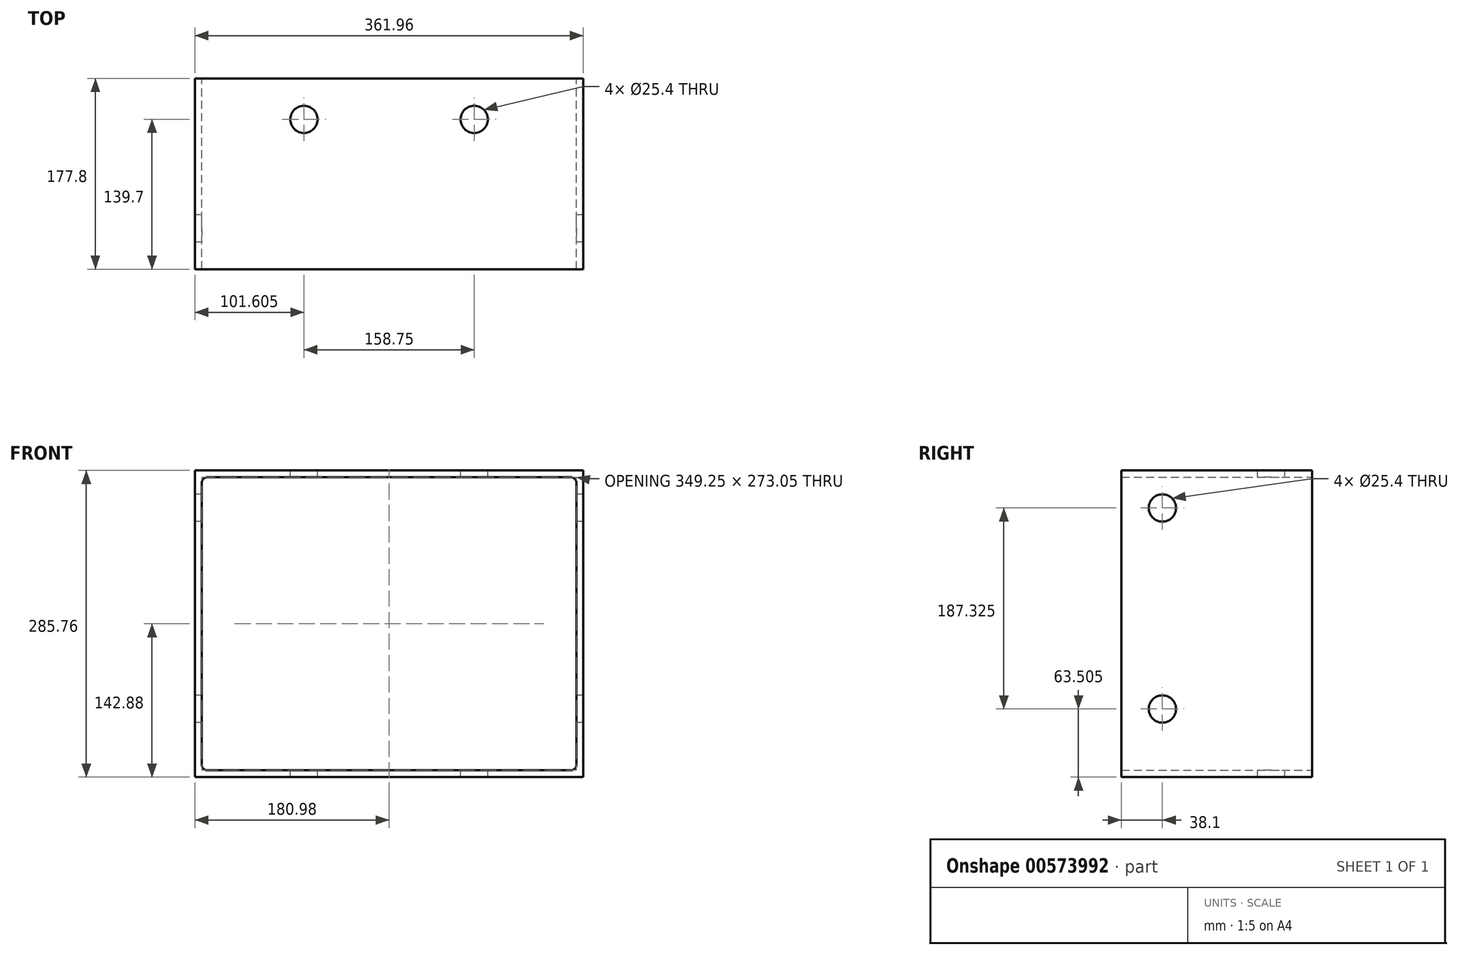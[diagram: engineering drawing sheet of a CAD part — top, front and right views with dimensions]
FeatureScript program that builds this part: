
annotation { "Feature Type Name" : "Feature", "Feature Type Description" : "" }
export const myFeature = defineFeature(function(context is Context, id is Id, definition is map)
    precondition{}
    {
        {
            var Q0;
            Q0=qCreatedBy(makeId("Front.planeOp"),FACE);
            var sketch = newSketch(context, id + "F0", { "sketchPlane" : qUnion([Q0])});
            skLineSegment(sketch, "E0.bottom", {"start": v(174.62, 136.53) * mm, "end": v(-174.63, 136.53) * mm});
            skLineSegment(sketch, "E0.top", {"start": v(174.63, -136.53) * mm, "end": v(-174.63, -136.53) * mm});
            skLineSegment(sketch, "E0.left", {"start": v(174.62, 136.53) * mm, "end": v(174.63, -136.52) * mm});
            skLineSegment(sketch, "E0.right", {"start": v(-174.63, 136.52) * mm, "end": v(-174.63, -136.53) * mm});
            skPoint(sketch, "E0.middle", {"position": v(0, 0) * mm});
            skLineSegment(sketch, "E1.bottom", {"start": v(-180.98, -142.88) * mm, "end": v(180.97, -142.88) * mm});
            skLineSegment(sketch, "E1.top", {"start": v(-180.97, 142.88) * mm, "end": v(180.98, 142.88) * mm});
            skLineSegment(sketch, "E1.left", {"start": v(-180.98, -142.88) * mm, "end": v(-180.97, 142.88) * mm});
            skLineSegment(sketch, "E1.right", {"start": v(180.98, -142.88) * mm, "end": v(180.98, 142.87) * mm});
            skSolve(sketch);
        }
        {
            var Q0;
            Q0=makeQuery(id+"F0.imprint","IMPRINT",FACE,{"disambiguationData":[TD([[makeQuery(id+"F0.imprint","IMPRINT",EDGE,{"derivedFrom":sQuery(id+"F0.wireOp",EDGE,"E0.bottom")}),-1.0]])]});
            extrude(context, id + "F1", {"entities" : qUnion([Q0]), "endBound" : BoundingType.SYMMETRIC, "depth" : 177.8 * mm, "offsetDistance" : 25.4 * mm});
        }
        {
            var Q0;
            Q0=makeQuery(id+"F1.opExtrude","SWEPT_EDGE",EDGE,{"disambiguationData":[OSD([sQuery(id+"F0.wireOp",EDGE,"E0.top"),sQuery(id+"F0.wireOp",EDGE,"E0.right")])]});
            var Q1;
            Q1=makeQuery(id+"F1.opExtrude","SWEPT_EDGE",EDGE,{"disambiguationData":[OSD([sQuery(id+"F0.wireOp",EDGE,"E0.top"),sQuery(id+"F0.wireOp",EDGE,"E0.left")])]});
            var Q2;
            Q2=makeQuery(id+"F1.opExtrude","SWEPT_EDGE",EDGE,{"disambiguationData":[OSD([sQuery(id+"F0.wireOp",EDGE,"E0.bottom"),sQuery(id+"F0.wireOp",EDGE,"E0.left")])]});
            var Q3;
            Q3=makeQuery(id+"F1.opExtrude","SWEPT_EDGE",EDGE,{"disambiguationData":[OSD([sQuery(id+"F0.wireOp",EDGE,"E0.bottom"),sQuery(id+"F0.wireOp",EDGE,"E0.right")])]});
            fillet(context, id + "F2", {"entities" : qUnion([Q0, Q1, Q2, Q3]), "radius" : 5.08 * mm, "tangentPropagation" : true, "allowEdgeOverflow" : false});
        }
        {
            var Q0;
            Q0=makeQuery(id+"F1.opExtrude","SWEPT_FACE",FACE,{"disambiguationData":[OSD([sQuery(id+"F0.wireOp",EDGE,"E1.top")])]});
            var sketch = newSketch(context, id + "F3", { "sketchPlane" : qUnion([Q0])});
            skCircle(sketch, "E2", {"center": v(-79.38, 50.8) * mm, "radius": 12.7 * mm});
            skCircle(sketch, "E3", {"center": v(79.38, 50.8) * mm, "radius": 12.7 * mm});
            skCircle(sketch, "E4", {"center": v(-79.38, 50.8) * mm, "radius": 50.8 * mm, "construction": true});
            skCircle(sketch, "E5", {"center": v(79.38, 50.8) * mm, "radius": 50.8 * mm, "construction": true});
            skSolve(sketch);
        }
        {
            var Q0;
            Q0=sQuery(id+"F3.wireOp",VERTEX,"E2.center");
            var Q1;
            Q1=sQuery(id+"F3.wireOp",VERTEX,"E3.center");
            var Q2;
            Q2=makeQuery(id+"F1.opExtrude","SWEPT_BODY",BODY,{"disambiguationData":[OSD([sQuery(id+"F0.wireOp",EDGE,"E0.bottom"),sQuery(id+"F0.wireOp",EDGE,"E0.top"),sQuery(id+"F0.wireOp",EDGE,"E0.left"),sQuery(id+"F0.wireOp",EDGE,"E0.right"),sQuery(id+"F0.wireOp",EDGE,"E1.bottom"),sQuery(id+"F0.wireOp",EDGE,"E1.top"),sQuery(id+"F0.wireOp",EDGE,"E1.left"),sQuery(id+"F0.wireOp",EDGE,"E1.right")])]});
            hole(context, id + "F4", {"style" : HoleStyle.SIMPLE, "endStyle" : HoleEndStyle.THROUGH, "holeDiameter" : 25.4 * mm, "isTappedThrough" : true, "tappedDepth" : 12.7 * mm, "tapClearance" : 3, "locations" : qUnion([Q0, Q1]), "scope" : qUnion([Q2]), "majorDiameter" : 6.35 * mm});
        }
        {
            var Q0;
            Q0=makeQuery(id+"F1.opExtrude","SWEPT_FACE",FACE,{"disambiguationData":[OSD([sQuery(id+"F0.wireOp",EDGE,"E1.left")])]});
            var sketch = newSketch(context, id + "F5", { "sketchPlane" : qUnion([Q0])});
            skCircle(sketch, "E6", {"center": v(50.8, 107.95) * mm, "radius": 12.7 * mm});
            skCircle(sketch, "E7", {"center": v(50.8, -79.38) * mm, "radius": 12.7 * mm});
            skLineSegment(sketch, "E8.bottom", {"start": v(88.9, 142.88) * mm, "end": v(10.27, 142.88) * mm, "construction": true});
            skLineSegment(sketch, "E8.top", {"start": v(88.9, 107.95) * mm, "end": v(10.27, 107.95) * mm, "construction": true});
            skLineSegment(sketch, "E8.left", {"start": v(88.9, 142.88) * mm, "end": v(88.9, 107.95) * mm, "construction": true});
            skLineSegment(sketch, "E8.right", {"start": v(10.27, 142.88) * mm, "end": v(10.27, 107.95) * mm, "construction": true});
            skCircle(sketch, "E9", {"center": v(50.8, 107.95) * mm, "radius": 25.4 * mm, "construction": true});
            skPoint(sketch, "E10.oppositeSnap0", {"position": v(10.27, 125.41) * mm});
            skLineSegment(sketch, "E10.bottom", {"start": v(88.9, 142.88) * mm, "end": v(10.27, 142.88) * mm});
            skLineSegment(sketch, "E10.top", {"start": v(88.9, -27.6) * mm, "end": v(10.27, -27.6) * mm});
            skLineSegment(sketch, "E10.left", {"start": v(88.9, 142.88) * mm, "end": v(88.9, -27.6) * mm});
            skLineSegment(sketch, "E10.right", {"start": v(10.27, 142.88) * mm, "end": v(10.27, -27.6) * mm});
            skCircle(sketch, "E11", {"center": v(50.8, -79.38) * mm, "radius": 50.8 * mm, "construction": true});
            skSolve(sketch);
        }
        {
            var Q0;
            Q0=sQuery(id+"F5.wireOp",VERTEX,"E6.center");
            var Q1;
            Q1=sQuery(id+"F5.wireOp",VERTEX,"E7.center");
            var Q2;
            Q2=makeQuery(id+"F1.opExtrude","SWEPT_BODY",BODY,{"disambiguationData":[OSD([sQuery(id+"F0.wireOp",EDGE,"E0.bottom"),sQuery(id+"F0.wireOp",EDGE,"E0.top"),sQuery(id+"F0.wireOp",EDGE,"E0.left"),sQuery(id+"F0.wireOp",EDGE,"E0.right"),sQuery(id+"F0.wireOp",EDGE,"E1.bottom"),sQuery(id+"F0.wireOp",EDGE,"E1.top"),sQuery(id+"F0.wireOp",EDGE,"E1.left"),sQuery(id+"F0.wireOp",EDGE,"E1.right")])]});
            hole(context, id + "F6", {"style" : HoleStyle.SIMPLE, "endStyle" : HoleEndStyle.THROUGH, "holeDiameter" : 25.4 * mm, "majorDiameter" : 6.35 * mm, "isTappedThrough" : true, "tappedDepth" : 12.7 * mm, "tapClearance" : 3, "locations" : qUnion([Q0, Q1]), "scope" : qUnion([Q2])});
        }
    });
